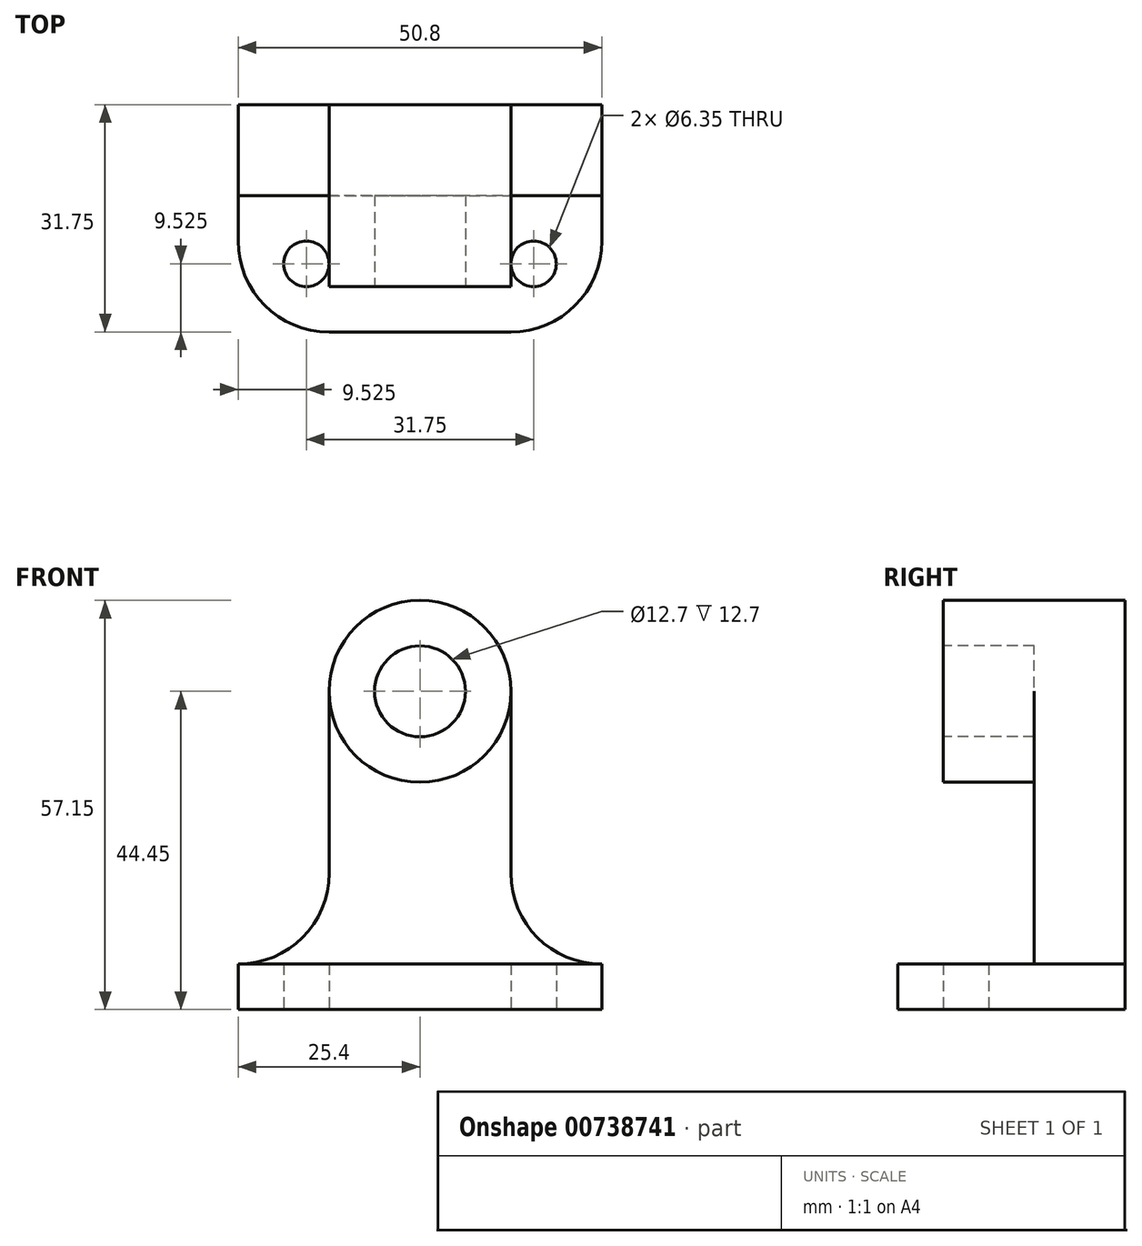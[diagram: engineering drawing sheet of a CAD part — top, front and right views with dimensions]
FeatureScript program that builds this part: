
annotation { "Feature Type Name" : "Feature", "Feature Type Description" : "" }
export const myFeature = defineFeature(function(context is Context, id is Id, definition is map)
    precondition{}
    {
        {
            var Q0;
            Q0=qCreatedBy(makeId("Top.planeOp"),FACE);
            var sketch = newSketch(context, id + "F0", { "sketchPlane" : qUnion([Q0])});
            skLineSegment(sketch, "E0", {"start": v(0, 0) * mm, "end": v(0, 31.75) * mm});
            skLineSegment(sketch, "E1", {"start": v(0, 31.75) * mm, "end": v(50.8, 31.75) * mm});
            skLineSegment(sketch, "E2", {"start": v(50.8, 31.75) * mm, "end": v(50.8, 0) * mm});
            skLineSegment(sketch, "E3", {"start": v(50.8, 0) * mm, "end": v(0, 0) * mm});
            skSolve(sketch);
        }
        {
            var Q0;
            Q0 = qSketchRegion(id + "F0", true);
            extrude(context, id + "F1", {"entities" : qUnion([Q0]), "depth" : 57.15 * mm, "offsetDistance" : 25.4 * mm});
        }
        {
            var Q0;
            Q0=makeQuery(id+"F1.opExtrude","SWEPT_FACE",FACE,{"disambiguationData":[OSD([sQuery(id+"F0.wireOp",EDGE,"E3")])]});
            var sketch = newSketch(context, id + "F2", { "sketchPlane" : qUnion([Q0])});
            skLineSegment(sketch, "E4", {"start": v(0, 31.75) * mm, "end": v(50.8, 31.75) * mm});
            skLineSegment(sketch, "E5", {"start": v(50.8, 31.75) * mm, "end": v(50.8, 6.35) * mm});
            skLineSegment(sketch, "E6", {"start": v(50.8, 6.35) * mm, "end": v(0, 6.35) * mm});
            skLineSegment(sketch, "E7", {"start": v(0, 6.35) * mm, "end": v(0, 31.75) * mm});
            skSolve(sketch);
        }
        {
            var Q0;
            Q0 = qSketchRegion(id + "F2", true);
            extrude(context, id + "F3", {"entities" : qUnion([Q0]), "operationType" : NewBodyOperationType.REMOVE, "oppositeDirection" : true, "depth" : 19.05 * mm, "offsetDistance" : 25.4 * mm});
        }
        {
            var Q0;
            {var subQ1=sQuery(id+"F0.wireOp",EDGE,"E3");Q0=makeQuery(id+"F3.boolean.opBoolean","SPLIT",FACE,{"disambiguationData":[TD([makeQuery(id+"F3.opExtrude","SWEPT_FACE",FACE,{"disambiguationData":[OSD([sQuery(id+"F2.wireOp",EDGE,"E4")])]})])],"derivedFrom":makeQuery(id+"F1.opExtrude","SWEPT_FACE",FACE,{"disambiguationData":[OSD([subQ1])]})});}
            var sketch = newSketch(context, id + "F4", { "sketchPlane" : qUnion([Q0])});
            skLineSegment(sketch, "E8", {"start": v(0, 44.45) * mm, "end": v(50.8, 44.45) * mm});
            skCircle(sketch, "E9", {"center": v(25.4, 44.45) * mm, "radius": 12.7 * mm});
            skCircle(sketch, "E10", {"center": v(25.4, 44.45) * mm, "radius": 6.35 * mm});
            skSolve(sketch);
        }
        {
            var Q0;
            {var subQ0=sQuery(id+"F4.wireOp",EDGE,"E8");var subQ5=sQuery(id+"F4.wireOp",EDGE,"E9");var subQ6=makeQuery(id+"F4.imprint","INTERSECT",VERTEX,{"disambiguationData":[OD(0.0)],"derivedFrom":[subQ0,subQ5]});Q0=makeQuery(id+"F4.imprint","IMPRINT",FACE,{"disambiguationData":[TD([[makeQuery(id+"F4.imprint","IMPRINT",EDGE,{"disambiguationData":[TD([[subQ6,1.0]])],"derivedFrom":subQ5}),-1.0]])]});}
            var Q1;
            {var subQ0=sQuery(id+"F4.wireOp",EDGE,"E8");var subQ6=sQuery(id+"F4.wireOp",EDGE,"E9");var subQ7=makeQuery(id+"F4.imprint","INTERSECT",VERTEX,{"disambiguationData":[OD(0.0)],"derivedFrom":[subQ0,subQ6]});Q1=makeQuery(id+"F4.imprint","IMPRINT",FACE,{"disambiguationData":[TD([[makeQuery(id+"F4.imprint","IMPRINT",EDGE,{"disambiguationData":[TD([[subQ7,-1.0]])],"derivedFrom":subQ6}),-1.0]])]});}
            var Q2;
            {var subQ0=sQuery(id+"F4.wireOp",EDGE,"E8");var subQ6=sQuery(id+"F4.wireOp",EDGE,"E9");var subQ7=makeQuery(id+"F4.imprint","INTERSECT",VERTEX,{"disambiguationData":[OD(1.0)],"derivedFrom":[subQ0,subQ6]});Q2=makeQuery(id+"F4.imprint","IMPRINT",FACE,{"disambiguationData":[TD([[makeQuery(id+"F4.imprint","IMPRINT",EDGE,{"disambiguationData":[TD([[subQ7,1.0]])],"derivedFrom":subQ6}),-1.0]])]});}
            var Q3;
            {var subQ0=sQuery(id+"F4.wireOp",EDGE,"E8");var subQ5=sQuery(id+"F4.wireOp",EDGE,"E9");var subQ6=makeQuery(id+"F4.imprint","INTERSECT",VERTEX,{"disambiguationData":[OD(1.0)],"derivedFrom":[subQ0,subQ5]});Q3=makeQuery(id+"F4.imprint","IMPRINT",FACE,{"disambiguationData":[TD([[makeQuery(id+"F4.imprint","IMPRINT",EDGE,{"disambiguationData":[TD([[subQ6,-1.0]])],"derivedFrom":subQ5}),-1.0]])]});}
            var Q4;
            {var subQ0=sQuery(id+"F4.wireOp",EDGE,"E10");var subQ1=sQuery(id+"F4.wireOp",EDGE,"E8");var subQ2=makeQuery(id+"F4.imprint","INTERSECT",VERTEX,{"disambiguationData":[OD(0.0)],"derivedFrom":[subQ1,subQ0]});Q4=makeQuery(id+"F4.imprint","IMPRINT",FACE,{"disambiguationData":[TD([[makeQuery(id+"F4.imprint","IMPRINT",EDGE,{"disambiguationData":[TD([[subQ2,-1.0]])],"derivedFrom":subQ1}),1.0]])]});}
            var Q5;
            {var subQ0=sQuery(id+"F4.wireOp",EDGE,"E10");var subQ1=sQuery(id+"F4.wireOp",EDGE,"E8");var subQ2=makeQuery(id+"F4.imprint","INTERSECT",VERTEX,{"disambiguationData":[OD(0.0)],"derivedFrom":[subQ1,subQ0]});Q5=makeQuery(id+"F4.imprint","IMPRINT",FACE,{"disambiguationData":[TD([[makeQuery(id+"F4.imprint","IMPRINT",EDGE,{"disambiguationData":[TD([[subQ2,-1.0]])],"derivedFrom":subQ1}),-1.0]])]});}
            extrude(context, id + "F5", {"entities" : qUnion([Q0, Q1, Q2, Q3, Q4, Q5]), "operationType" : NewBodyOperationType.REMOVE, "oppositeDirection" : true, "depth" : 19.05 * mm, "offsetDistance" : 25.4 * mm});
        }
        {
            var Q0;
            {var subQ1=sQuery(id+"F0.wireOp",EDGE,"E3");Q0=makeQuery(id+"F3.boolean.opBoolean","SPLIT",FACE,{"disambiguationData":[TD([makeQuery(id+"F3.opExtrude","SWEPT_FACE",FACE,{"disambiguationData":[OSD([sQuery(id+"F2.wireOp",EDGE,"E4")])]})])],"derivedFrom":makeQuery(id+"F1.opExtrude","SWEPT_FACE",FACE,{"disambiguationData":[OSD([subQ1])]})});}
            extrude(context, id + "F6", {"entities" : qUnion([Q0]), "operationType" : NewBodyOperationType.REMOVE, "oppositeDirection" : true, "depth" : 6.35 * mm, "offsetDistance" : 25.4 * mm});
        }
        {
            var Q0;
            Q0=makeQuery(id+"F1.opExtrude","CAP_FACE",FACE,{"disambiguationData":[OSD([sQuery(id+"F0.wireOp",EDGE,"E0"),sQuery(id+"F0.wireOp",EDGE,"E1"),sQuery(id+"F0.wireOp",EDGE,"E2"),sQuery(id+"F0.wireOp",EDGE,"E3")])],"isStart":true});
            var sketch = newSketch(context, id + "F7", { "sketchPlane" : qUnion([Q0])});
            skLineSegment(sketch, "E11", {"start": v(0, -12.7) * mm, "end": v(12.7, -12.7) * mm});
            skLineSegment(sketch, "E12", {"start": v(12.7, -12.7) * mm, "end": v(12.7, 0) * mm});
            skLineSegment(sketch, "E13", {"start": v(50.8, -12.7) * mm, "end": v(38.1, -12.7) * mm});
            skLineSegment(sketch, "E14", {"start": v(38.1, -12.7) * mm, "end": v(38.1, 0) * mm});
            skCircle(sketch, "E15", {"center": v(12.7, -12.7) * mm, "radius": 12.7 * mm});
            skCircle(sketch, "E16", {"center": v(38.1, -12.7) * mm, "radius": 12.7 * mm});
            skSolve(sketch);
        }
        {
            var Q0;
            {var subQ1=makeQuery(id+"F1.opExtrude","CAP_EDGE",EDGE,{"disambiguationData":[OSD([sQuery(id+"F0.wireOp",EDGE,"E0")])],"isStart":true});var subQ3=makeQuery(id+"F1.opExtrude","CAP_EDGE",EDGE,{"disambiguationData":[OSD([sQuery(id+"F0.wireOp",EDGE,"E3")])],"isStart":true});var subQ5=makeQuery(id+"F7.imprint","INTERSECT",VERTEX,{"derivedFrom":[subQ1,subQ3]});Q0=makeQuery(id+"F7.imprint","IMPRINT",FACE,{"disambiguationData":[TD([[makeQuery(id+"F7.imprint","IMPRINT",EDGE,{"disambiguationData":[TD([[subQ5,-1.0]])],"derivedFrom":subQ1}),1.0]])]});}
            var Q1;
            {var subQ1=makeQuery(id+"F1.opExtrude","CAP_EDGE",EDGE,{"disambiguationData":[OSD([sQuery(id+"F0.wireOp",EDGE,"E2")])],"isStart":true});var subQ3=makeQuery(id+"F1.opExtrude","CAP_EDGE",EDGE,{"disambiguationData":[OSD([sQuery(id+"F0.wireOp",EDGE,"E3")])],"isStart":true});var subQ5=makeQuery(id+"F7.imprint","INTERSECT",VERTEX,{"derivedFrom":[subQ1,subQ3]});Q1=makeQuery(id+"F7.imprint","IMPRINT",FACE,{"disambiguationData":[TD([[makeQuery(id+"F7.imprint","IMPRINT",EDGE,{"disambiguationData":[TD([[subQ5,1.0]])],"derivedFrom":subQ1}),1.0]])]});}
            extrude(context, id + "F8", {"entities" : qUnion([Q0, Q1]), "operationType" : NewBodyOperationType.REMOVE, "endBound" : BoundingType.THROUGH_ALL, "oppositeDirection" : true, "depth" : 25.4 * mm, "offsetDistance" : 25.4 * mm});
        }
        {
            var Q0;
            {var subQ0=sQuery(id+"F4.wireOp",EDGE,"E9");var subQ1=sQuery(id+"F2.wireOp",EDGE,"E4");var subQ2=sQuery(id+"F0.wireOp",EDGE,"E3");Q0=makeQuery(id+"F5.boolean.opBoolean","MERGE",FACE,{"derivedFrom":[makeQuery(id+"F3.boolean.opBoolean","COPY",FACE,{"derivedFrom":makeQuery(id+"F3.opExtrude","CAP_FACE",FACE,{"disambiguationData":[OSD([subQ1,sQuery(id+"F2.wireOp",EDGE,"E5"),sQuery(id+"F2.wireOp",EDGE,"E6"),sQuery(id+"F2.wireOp",EDGE,"E7")])],"isStart":false})}),makeQuery(id+"F5.opExtrude","CAP_FACE",FACE,{"disambiguationData":[OSD([sQuery(id+"F0.wireOp",EDGE,"E2"),subQ2,subQ1,subQ0])],"isStart":false}),makeQuery(id+"F5.opExtrude","CAP_FACE",FACE,{"disambiguationData":[OSD([sQuery(id+"F0.wireOp",EDGE,"E0"),subQ2,subQ1,subQ0])],"isStart":false})]});}
            var sketch = newSketch(context, id + "F9", { "sketchPlane" : qUnion([Q0])});
            skLineSegment(sketch, "E17", {"start": v(12.7, 57.15) * mm, "end": v(12.7, 19.05) * mm});
            skLineSegment(sketch, "E18", {"start": v(12.7, 19.05) * mm, "end": v(0, 19.05) * mm});
            skLineSegment(sketch, "E19", {"start": v(50.8, 19.05) * mm, "end": v(38.1, 19.05) * mm});
            skLineSegment(sketch, "E20", {"start": v(38.1, 19.05) * mm, "end": v(38.1, 57.15) * mm});
            skLineSegment(sketch, "E21", {"start": v(38.1, 57.15) * mm, "end": v(12.7, 57.15) * mm});
            skSolve(sketch);
        }
        {
            var Q0;
            {var subQ11=sQuery(id+"F9.wireOp",EDGE,"E18");Q0=makeQuery(id+"F9.imprint","IMPRINT",FACE,{"disambiguationData":[TD([[makeQuery(id+"F9.imprint","IMPRINT",EDGE,{"derivedFrom":subQ11}),-1.0]])]});}
            var Q1;
            {var subQ16=sQuery(id+"F9.wireOp",EDGE,"E19");Q1=makeQuery(id+"F9.imprint","IMPRINT",FACE,{"disambiguationData":[TD([[makeQuery(id+"F9.imprint","IMPRINT",EDGE,{"derivedFrom":subQ16}),-1.0]])]});}
            var Q2;
            {var subQ0=sQuery(id+"F9.wireOp",EDGE,"E21");var subQ1=sQuery(id+"F9.wireOp",EDGE,"E20");var subQ2=sQuery(id+"F0.wireOp",EDGE,"E3");var subQ5=makeQuery(id+"F1.opExtrude","CAP_EDGE",EDGE,{"disambiguationData":[OSD([subQ2])],"isStart":false});var subQ6=sQuery(id+"F4.wireOp",EDGE,"E9");var subQ7=makeQuery(id+"F4.imprint","INTERSECT",VERTEX,{"derivedFrom":[subQ5,subQ6]});var subQ8=makeQuery(id+"F9.imprint","INTERSECT",VERTEX,{"derivedFrom":[makeQuery(id+"F5.boolean.opBoolean","COPY",EDGE,{"derivedFrom":makeQuery(id+"F5.opExtrude","CAP_EDGE",EDGE,{"disambiguationData":[OSD([subQ2]),TDD([makeQuery(id+"F4.imprint","IMPRINT",EDGE,{"disambiguationData":[TD([[subQ7,1.0]])],"derivedFrom":subQ5})])],"isStart":false})}),subQ1,subQ0]});Q2=makeQuery(id+"F9.imprint","IMPRINT",FACE,{"disambiguationData":[TD([[makeQuery(id+"F9.imprint","IMPRINT",EDGE,{"disambiguationData":[TD([[subQ8,1.0]])],"derivedFrom":subQ1}),1.0]])]});}
            var Q3;
            {var subQ0=sQuery(id+"F9.wireOp",EDGE,"E21");var subQ1=sQuery(id+"F9.wireOp",EDGE,"E17");var subQ3=sQuery(id+"F0.wireOp",EDGE,"E3");var subQ5=makeQuery(id+"F1.opExtrude","CAP_EDGE",EDGE,{"disambiguationData":[OSD([subQ3])],"isStart":false});var subQ6=sQuery(id+"F4.wireOp",EDGE,"E9");var subQ7=makeQuery(id+"F4.imprint","INTERSECT",VERTEX,{"derivedFrom":[subQ5,subQ6]});var subQ8=makeQuery(id+"F9.imprint","INTERSECT",VERTEX,{"derivedFrom":[makeQuery(id+"F5.boolean.opBoolean","COPY",EDGE,{"derivedFrom":makeQuery(id+"F5.opExtrude","CAP_EDGE",EDGE,{"disambiguationData":[OSD([subQ3]),TDD([makeQuery(id+"F4.imprint","IMPRINT",EDGE,{"disambiguationData":[TD([[subQ7,-1.0]])],"derivedFrom":subQ5})])],"isStart":false})}),subQ1,subQ0]});Q3=makeQuery(id+"F9.imprint","IMPRINT",FACE,{"disambiguationData":[TD([[makeQuery(id+"F9.imprint","IMPRINT",EDGE,{"disambiguationData":[TD([[subQ8,-1.0]])],"derivedFrom":subQ1}),1.0]])]});}
            extrude(context, id + "F10", {"entities" : qUnion([Q0, Q1, Q2, Q3]), "operationType" : NewBodyOperationType.REMOVE, "endBound" : BoundingType.THROUGH_ALL, "oppositeDirection" : true, "depth" : 25.4 * mm, "offsetDistance" : 25.4 * mm});
        }
        {
            var Q0;
            {var subQ0=sQuery(id+"F4.wireOp",EDGE,"E9");var subQ1=sQuery(id+"F2.wireOp",EDGE,"E4");var subQ2=sQuery(id+"F0.wireOp",EDGE,"E3");Q0=makeQuery(id+"F5.boolean.opBoolean","MERGE",FACE,{"derivedFrom":[makeQuery(id+"F3.boolean.opBoolean","COPY",FACE,{"derivedFrom":makeQuery(id+"F3.opExtrude","CAP_FACE",FACE,{"disambiguationData":[OSD([subQ1,sQuery(id+"F2.wireOp",EDGE,"E5"),sQuery(id+"F2.wireOp",EDGE,"E6"),sQuery(id+"F2.wireOp",EDGE,"E7")])],"isStart":false})}),makeQuery(id+"F5.opExtrude","CAP_FACE",FACE,{"disambiguationData":[OSD([sQuery(id+"F0.wireOp",EDGE,"E2"),subQ2,subQ1,subQ0])],"isStart":false}),makeQuery(id+"F5.opExtrude","CAP_FACE",FACE,{"disambiguationData":[OSD([sQuery(id+"F0.wireOp",EDGE,"E0"),subQ2,subQ1,subQ0])],"isStart":false})]});}
            var sketch = newSketch(context, id + "F11", { "sketchPlane" : qUnion([Q0])});
            skArc(sketch, "E22", {"start": v(0, 6.35) * mm, "mid": v(8.98, 10.07) * mm, "end": v(12.7, 19.05) * mm});
            skArc(sketch, "E23", {"start": v(38.1, 19.05) * mm, "mid": v(41.82, 10.07) * mm, "end": v(50.8, 6.35) * mm});
            skSolve(sketch);
        }
        {
            var Q0;
            Q0=makeQuery(id+"F11.imprint","IMPRINT",FACE,{"disambiguationData":[TD([[makeQuery(id+"F11.imprint","IMPRINT",EDGE,{"derivedFrom":sQuery(id+"F11.wireOp",EDGE,"E22")}),1.0]])]});
            var Q1;
            Q1=makeQuery(id+"F11.imprint","IMPRINT",FACE,{"disambiguationData":[TD([[makeQuery(id+"F11.imprint","IMPRINT",EDGE,{"derivedFrom":sQuery(id+"F11.wireOp",EDGE,"E23")}),1.0]])]});
            extrude(context, id + "F12", {"entities" : qUnion([Q0, Q1]), "operationType" : NewBodyOperationType.REMOVE, "endBound" : BoundingType.THROUGH_ALL, "oppositeDirection" : true, "depth" : 25.4 * mm, "offsetDistance" : 25.4 * mm});
        }
        {
            var Q0;
            Q0=makeQuery(id+"F1.opExtrude","CAP_FACE",FACE,{"disambiguationData":[OSD([sQuery(id+"F0.wireOp",EDGE,"E0"),sQuery(id+"F0.wireOp",EDGE,"E1"),sQuery(id+"F0.wireOp",EDGE,"E2"),sQuery(id+"F0.wireOp",EDGE,"E3")])],"isStart":true});
            var sketch = newSketch(context, id + "F13", { "sketchPlane" : qUnion([Q0])});
            skLineSegment(sketch, "E24", {"start": v(0, -9.53) * mm, "end": v(9.52, -9.53) * mm});
            skLineSegment(sketch, "E25", {"start": v(9.52, -9.53) * mm, "end": v(9.52, 0) * mm});
            skLineSegment(sketch, "E26", {"start": v(41.27, 0) * mm, "end": v(41.27, -9.52) * mm});
            skLineSegment(sketch, "E27", {"start": v(41.27, -9.52) * mm, "end": v(50.8, -9.52) * mm});
            skCircle(sketch, "E28", {"center": v(9.52, -9.53) * mm, "radius": 3.18 * mm});
            skCircle(sketch, "E29", {"center": v(41.27, -9.52) * mm, "radius": 3.18 * mm});
            skSolve(sketch);
        }
        {
            var Q0;
            {var subQ0=sQuery(id+"F13.wireOp",EDGE,"E25");var subQ1=sQuery(id+"F13.wireOp",EDGE,"E24");var subQ2=makeQuery(id+"F13.imprint","INTERSECT",VERTEX,{"derivedFrom":[subQ1,subQ0]});Q0=makeQuery(id+"F13.imprint","IMPRINT",FACE,{"disambiguationData":[TD([[makeQuery(id+"F13.imprint","IMPRINT",EDGE,{"disambiguationData":[TD([[subQ2,1.0]])],"derivedFrom":subQ1}),-1.0]])]});}
            var Q1;
            {var subQ0=sQuery(id+"F13.wireOp",EDGE,"E25");var subQ1=sQuery(id+"F13.wireOp",EDGE,"E24");var subQ2=makeQuery(id+"F13.imprint","INTERSECT",VERTEX,{"derivedFrom":[subQ1,subQ0]});Q1=makeQuery(id+"F13.imprint","IMPRINT",FACE,{"disambiguationData":[TD([[makeQuery(id+"F13.imprint","IMPRINT",EDGE,{"disambiguationData":[TD([[subQ2,1.0]])],"derivedFrom":subQ1}),1.0]])]});}
            var Q2;
            {var subQ0=sQuery(id+"F13.wireOp",EDGE,"E27");var subQ1=sQuery(id+"F13.wireOp",EDGE,"E26");var subQ2=makeQuery(id+"F13.imprint","INTERSECT",VERTEX,{"derivedFrom":[subQ1,subQ0]});Q2=makeQuery(id+"F13.imprint","IMPRINT",FACE,{"disambiguationData":[TD([[makeQuery(id+"F13.imprint","IMPRINT",EDGE,{"disambiguationData":[TD([[subQ2,1.0]])],"derivedFrom":subQ1}),-1.0]])]});}
            var Q3;
            {var subQ0=sQuery(id+"F13.wireOp",EDGE,"E27");var subQ1=sQuery(id+"F13.wireOp",EDGE,"E26");var subQ2=makeQuery(id+"F13.imprint","INTERSECT",VERTEX,{"derivedFrom":[subQ1,subQ0]});Q3=makeQuery(id+"F13.imprint","IMPRINT",FACE,{"disambiguationData":[TD([[makeQuery(id+"F13.imprint","IMPRINT",EDGE,{"disambiguationData":[TD([[subQ2,1.0]])],"derivedFrom":subQ1}),1.0]])]});}
            extrude(context, id + "F14", {"entities" : qUnion([Q0, Q1, Q2, Q3]), "operationType" : NewBodyOperationType.REMOVE, "oppositeDirection" : true, "depth" : 25.4 * mm, "offsetDistance" : 25.4 * mm});
        }
    });
